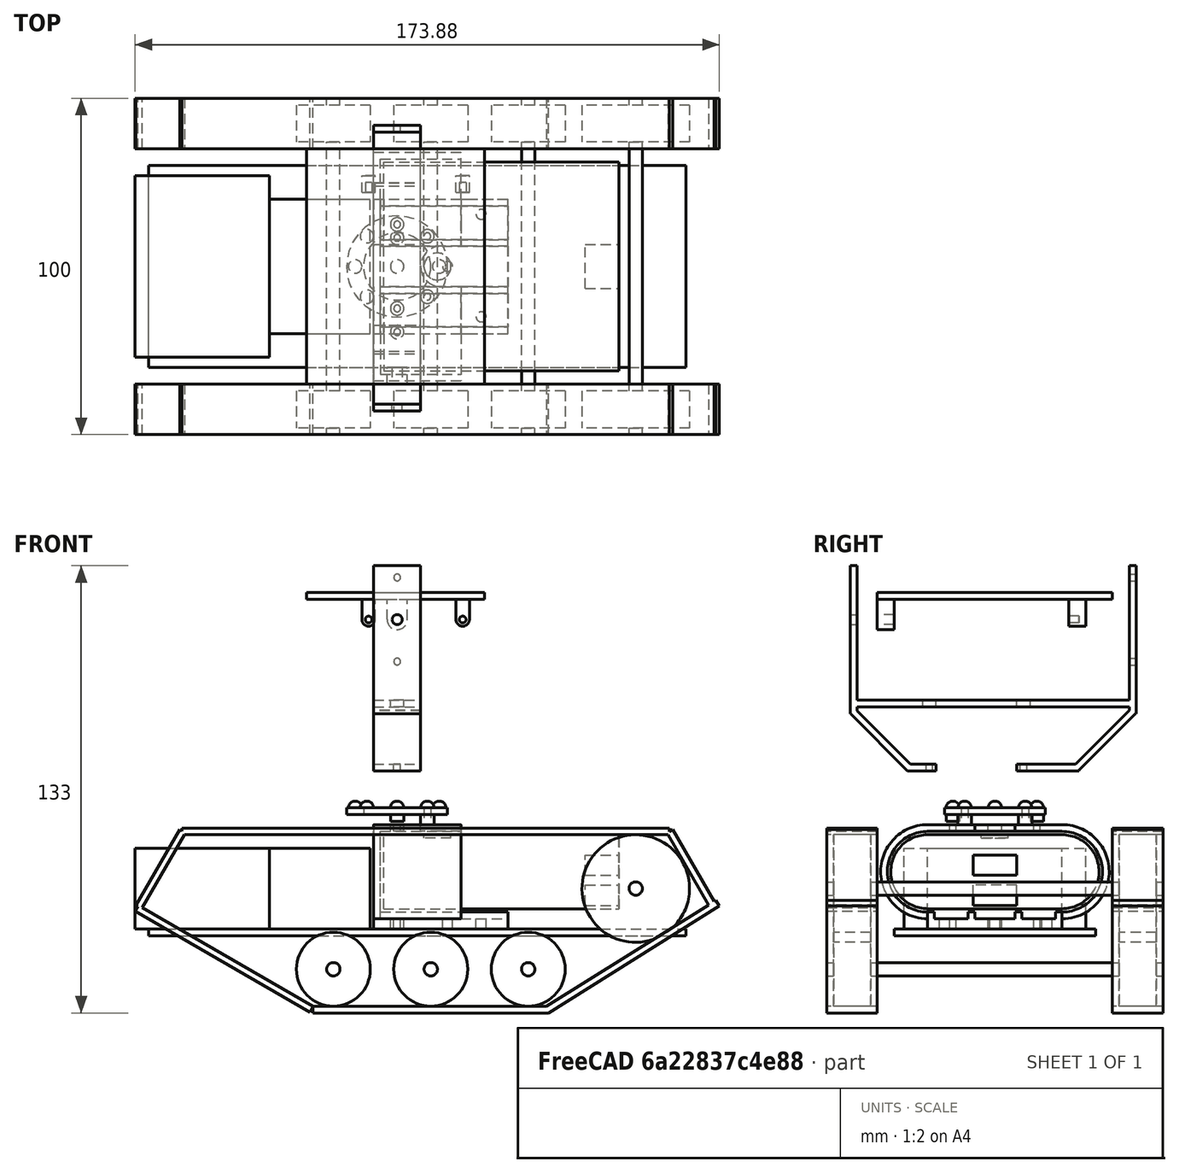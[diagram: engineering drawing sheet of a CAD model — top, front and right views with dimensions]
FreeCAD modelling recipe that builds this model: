
FCSTD DOCUMENT
Label: androidtank_4
License: CC-BY 3.0
LicenseURL: http://creativecommons.org/licenses/by/3.0/
objects: Part::Cylinder×43, Part::Box×31, Part::MultiFuse×17, Part::Sphere×8, Part::Cut×6, App::DocumentObjectGroup×1
note: 105 computed .brp shape members not serialized (recipe doc carries the construction recipe); baked Part::Feature solids carry a one-line shape summary decoded from their .brp

FEATURE [Part::Box] Box  label="MainFrame"
  Height = 2
  Length = 160
  Width = 60
FEATURE [Part::Box] Box001001  label="Moter Unit2"
  Height = 24
  Length = 30
  Placement = pos=(36,10,2) rot=(0,0,1;0rad)
  Width = 40
FEATURE [Part::Cylinder] Cylinder002  label="Wheel1"
  Angle = 360
  Height = 11
  Placement = pos=(20,-7,14) rot=(1,0,0;1.5708rad)
  Radius = 16
FEATURE [Part::Cylinder] Cylinder  label="Shaft"
  Angle = 360
  Height = 100
  Placement = pos=(20,-20,14) rot=(-1,0,0;1.5708rad)
  Radius = 2
FEATURE [Part::Cylinder] Cylinder002001  label="Wheel2"
  Angle = 360
  Height = 11
  Placement = pos=(20,78,14) rot=(1,0,0;1.5708rad)
  Radius = 16
FEATURE [Part::MultiFuse] Fusion001  label="WheelSet2"
  Placement = pos=(125,0,0) rot=(0,0,1;0rad)
  Shapes = -> [Cylinder,Cylinder002,Cylinder002001]
FEATURE [Part::Box] Box001002
  Height = 2
  Length = 145
  Placement = pos=(10,-20,30) rot=(0,0,1;0rad)
  Width = 15
FEATURE [Part::Box] Box001002001
  Height = 2
  Length = 70
  Placement = pos=(49,-20,-23) rot=(0,0,1;0rad)
  Width = 15
FEATURE [Part::Box] Box001002001001
  Height = 2
  Length = 60
  Placement = pos=(119,-20,-23) rot=(0,-1,0;0.558505rad)
  Width = 15
FEATURE [Part::Box] Box001002001002
  Height = 2
  Length = 60
  Placement = pos=(49,-20,-21) rot=(0,1,0;3.66519rad)
  Width = 15
FEATURE [Part::Box] Box001002001003
  Height = 2
  Length = 26
  Placement = pos=(-2,-20,8) rot=(0,-1,0;1.0472rad)
  Width = 15
FEATURE [Part::Box] Box001002001003001
  Height = 2
  Length = 26
  Placement = pos=(169,-20,9) rot=(0,-1,0;2.0944rad)
  Width = 15
FEATURE [Part::MultiFuse] Fusion002001002  label="Caterpiller1"
  Shapes = -> [Box001002,Box001002001,Box001002001002,Box001002001001,Box001002001003,Box001002001003001]
FEATURE [Part::MultiFuse] Fusion002001002001  label="Caterpiller2"
  Placement = pos=(0,85,0) rot=(0,0,1;0rad)
  Shapes = -> [Box001002,Box001002001,Box001002001002,Box001002001001,Box001002001003,Box001002001003001]
FEATURE [Part::Cylinder] Cylinder002001001002  label="Wheel006"
  Angle = 360
  Height = 11
  Placement = pos=(20,78,14) rot=(1,0,0;1.5708rad)
  Radius = 11
FEATURE [Part::Cylinder] Cylinder002001001002001  label="Wheel007"
  Angle = 360
  Height = 11
  Placement = pos=(20,-7,14) rot=(1,0,0;1.5708rad)
  Radius = 11
FEATURE [Part::Cylinder] Cylinder002001002001  label="Shaft002"
  Angle = 360
  Height = 100
  Placement = pos=(20,-20,14) rot=(-1,0,0;1.5708rad)
  Radius = 2
FEATURE [Part::MultiFuse] Fusion002001002002002  label="SWheelSet1"
  Placement = pos=(35,0,-24) rot=(0,0,1;0rad)
  Shapes = -> [Cylinder002001002001,Cylinder002001001002,Cylinder002001001002001]
FEATURE [Part::MultiFuse] Fusion002001002002002001  label="SWheelSet2"
  Placement = pos=(64,0,-24) rot=(0,0,1;0rad)
  Shapes = -> [Cylinder002001002001,Cylinder002001001002,Cylinder002001001002001]
FEATURE [Part::MultiFuse] Fusion002001002002002001001  label="SWheelSet3"
  Placement = pos=(93,0,-24) rot=(0,0,1;0rad)
  Shapes = -> [Cylinder002001002001,Cylinder002001001002,Cylinder002001001002001]
FEATURE [Part::Box] Box001002001003002
  Height = 22
  Length = 70
  Placement = pos=(0,0,-11) rot=(0,0,1;0rad)
  Width = 40
FEATURE [Part::Cylinder] Cylinder002001001002002
  Angle = 360
  Height = 70
  Placement = pos=(0,0,0) rot=(0,1,0;1.5708rad)
  Radius = 11
FEATURE [Part::Cylinder] Cylinder001
  Angle = 360
  Height = 70
  Placement = pos=(0,40,0) rot=(0,1,0;1.5708rad)
  Radius = 11
FEATURE [Part::Cylinder] Cylinder002001001002003  label="PowerButton"
  Angle = 360
  Height = 2
  Placement = pos=(16,20,10) rot=(0,0,1;0rad)
  Radius = 4
FEATURE [Part::Box] Box001002001003003  label="USB1"
  Height = 6
  Length = 15
  Placement = pos=(60,13.5,-1) rot=(0,0,1;0rad)
  Width = 13
FEATURE [Part::Box] Box001001001  label="USB2"
  Height = 6
  Length = 15
  Placement = pos=(60,13.5,-10) rot=(0,0,1;0rad)
  Width = 13
FEATURE [Part::MultiFuse] Fusion002001002002002001002
  Shapes = -> [Cylinder001,Box001002001003002,Cylinder002001001002002]
FEATURE [Part::MultiFuse] Fusion001001
  Shapes = -> [Box001001001,Cylinder002001001002003,Box001002001003003]
FEATURE [Part::Cut] Cut  label="Eneloop"
  Base = -> Fusion002001002002002001002
  Placement = pos=(70,10,19) rot=(0,0,1;0rad)
  Tool = -> Fusion001001
FEATURE [Part::Cylinder] Cylinder001001  label="Cylinder002"
  Angle = 360
  Height = 26
  Placement = pos=(0,50,19) rot=(0,1,0;1.5708rad)
  Radius = 14
FEATURE [Part::Box] Box001002001003002001  label="Box001002001003002001001001001006001001002001003001002"
  Height = 28
  Length = 26
  Placement = pos=(0,10,5) rot=(0,0,1;0rad)
  Width = 40
FEATURE [Part::Cylinder] Cylinder002001001002002001  label="Cylinder003"
  Angle = 360
  Height = 26
  Placement = pos=(0,10,19) rot=(0,1,0;1.5708rad)
  Radius = 14
FEATURE [Part::Box] Box001  label="Moter Unit1"
  Height = 24
  Length = 40
  Placement = pos=(-4,3,2) rot=(0,0,1;0rad)
  Width = 54
FEATURE [App::DocumentObjectGroup] ____________  label="DriveFrame"
  Group = -> [Box,Box001,Box001001,Fusion002001002,Fusion002001002001,Fusion002001002002002,Fusion002001002002002001,Fusion002001002002002001001,Fusion001]
FEATURE [Part::Box] Box001002001003002001001  label="Box003"
  Height = 5
  Length = 40
  Placement = pos=(0,10,2) rot=(0,0,1;0rad)
  Width = 40
FEATURE [Part::Box] Box001002001003002001002  label="Box004"
  Height = 24
  Length = 26
  Placement = pos=(2,10,7) rot=(0,0,1;0rad)
  Width = 40
FEATURE [Part::Cylinder] Cylinder001001001  label="Cylinder004"
  Angle = 360
  Height = 26
  Placement = pos=(2,50,19) rot=(0,1,0;1.5708rad)
  Radius = 12
FEATURE [Part::Cylinder] Cylinder002001001002002001001  label="Cylinder005"
  Angle = 360
  Height = 26
  Placement = pos=(2,10,19) rot=(0,1,0;1.5708rad)
  Radius = 12
FEATURE [Part::Cylinder] Cylinder002001001002003001  label="PowerButton001"
  Angle = 360
  Height = 4
  Placement = pos=(20,30,30) rot=(0,0,1;0rad)
  Radius = 6
FEATURE [Part::Box] Box001002001003002001003  label="Box005"
  Height = 4
  Length = 10
  Placement = pos=(20,24,30) rot=(0,0,1;0rad)
  Width = 12
FEATURE [Part::Box] Box001002001003002001001001  label="Box006"
  Height = 3
  Length = 40
  Placement = pos=(2,12,5) rot=(0,0,1;0rad)
  Width = 10
FEATURE [Part::Box] Box001002001003002001001001001  label="Box007"
  Height = 3
  Length = 40
  Placement = pos=(2,24,5) rot=(0,0,1;0rad)
  Width = 12
FEATURE [Part::Box] Box001002001003002001001001001001  label="Box008"
  Height = 3
  Length = 40
  Placement = pos=(2,38,5) rot=(0,0,1;0rad)
  Width = 10
FEATURE [Part::MultiFuse] Fusion002001002002002001003
  Shapes = -> [Box001002001003002001,Cylinder001001,Cylinder002001001002002001,Box001002001003002001001]
FEATURE [Part::MultiFuse] Fusion002001002002002001004
  Shapes = -> [Box001002001003002001002,Cylinder002001001002002001001,Cylinder001001001,Box001002001003002001001001001001,Box001002001003002001001001001,Box001002001003002001001001,Box001002001003002001003,Cylinder002001001002003001]
FEATURE [Part::Cut] Cut001  label="BatteryFrame"
  Base = -> Fusion002001002002002001003
  Placement = pos=(67,0,0) rot=(0,0,1;0rad)
  Tool = -> Fusion002001002002002001004
FEATURE [Part::Cylinder] Cylinder002001001002002001002001  label="Cylinder007"
  Angle = 360
  Height = 40
  Placement = pos=(74,17.5,0) rot=(0,0,1;0rad)
  Radius = 1
FEATURE [Part::Cylinder] Cylinder002001001002002001002  label="Cylinder006"
  Angle = 360
  Height = 40
  Placement = pos=(74,42.5,0) rot=(0,0,1;0rad)
  Radius = 1
FEATURE [Part::Cylinder] Cylinder002001001002002001002001001  label="Cylinder008"
  Angle = 360
  Height = 40
  Placement = pos=(89,30,0) rot=(0,0,1;0rad)
  Radius = 1.5
FEATURE [Part::Cylinder] Cylinder002001001002002001002001002  label="Cylinder009"
  Angle = 360
  Height = 40
  Placement = pos=(99,45.5,0) rot=(0,0,1;0rad)
  Radius = 1.5
FEATURE [Part::Cylinder] Cylinder002001001002002001002001003  label="Cylinder0010"
  Angle = 360
  Height = 40
  Placement = pos=(99,15,0) rot=(0,0,1;0rad)
  Radius = 1.5
FEATURE [Part::Box] Box001002001003002001001001001006  label="Box009"
  Height = 2
  Length = 53
  Placement = pos=(47,-5,100) rot=(0,0,1;0rad)
  Width = 70
FEATURE [Part::Box] Box001002001003002001001001001006001  label="Box010"
  Height = 44
  Length = 14
  Placement = pos=(67,70,66) rot=(0,0,1;0rad)
  Width = 2
FEATURE [Part::Box] Box001002001003002001001001001006001001  label="Box011"
  Height = 2
  Length = 13
  Placement = pos=(67.5,12.5,48) rot=(0,0,1;0rad)
  Width = 23.5
FEATURE [Part::Box] Box001002001003002001001001001006001001001  label="Box012"
  Height = 44
  Length = 14
  Placement = pos=(67,-13,66) rot=(0,0,1;0rad)
  Width = 2
FEATURE [Part::Cylinder] Cylinder002001001002002001002001008  label="Hole1"
  Angle = 360
  Height = 20
  Placement = pos=(74,-20,94) rot=(-1,0,0;1.5708rad)
  Radius = 1.5
FEATURE [Part::Cylinder] Cylinder002001001002002001002001008001  label="Hole2"
  Angle = 360
  Height = 20
  Placement = pos=(74,60,106.5) rot=(-1,0,0;1.5708rad)
  Radius = 1
FEATURE [Part::Cylinder] Cylinder002001001002002001002001008001001  label="Hole4"
  Angle = 360
  Height = 20
  Placement = pos=(74,38.5,41) rot=(0,0,1;0rad)
  Radius = 1
FEATURE [Part::Cylinder] Cylinder002001001002002001002001008001001001  label="Hole3"
  Angle = 360
  Height = 20
  Placement = pos=(74,60,81.5) rot=(-1,0,0;1.5708rad)
  Radius = 1
FEATURE [Part::Cylinder] Cylinder002001001002002001002001008001001002  label="Hole5"
  Angle = 360
  Height = 20
  Placement = pos=(74,10.5,41) rot=(0,0,1;0rad)
  Radius = 1
FEATURE [Part::Box] Box001002001003002001001001001006001001001001  label="Box013"
  Height = 24
  Length = 14
  Placement = pos=(67,4,49) rot=(1,0,0;0.785397rad)
  Width = 2
FEATURE [Part::Box] Box001002001003002001001001001006001001001001001  label="Box014"
  Height = 24
  Length = 14
  Placement = pos=(67,53.41,50.41) rot=(-1,0,0;0.785397rad)
  Width = 2
FEATURE [Part::Box] Box001002001003002001001001001006001001002001  label="Box016"
  Height = 2
  Length = 14
  Placement = pos=(67,4,49) rot=(0,0,1;0rad)
  Width = 8.5
FEATURE [Part::Box] Box001002001003002001001001001006001001002001001  label="Box017"
  Height = 2
  Length = 14
  Placement = pos=(67,36.5,49) rot=(0,0,1;0rad)
  Width = 18.5
FEATURE [Part::Box] Box001002001003002001001001001006001001002001002  label="Box015"
  Height = 2
  Length = 14
  Placement = pos=(67,-13,68) rot=(0,0,1;0rad)
  Width = 85
FEATURE [Part::MultiFuse] Fusion002001002002002001009
  Shapes = -> [Box001002001003002001001001001006001,Box001002001003002001001001001006001001001001,Box001002001003002001001001001006001001001,Box001002001003002001001001001006001001001001001,Box001002001003002001001001001006001001002001,Box001002001003002001001001001006001001002001002,Box001002001003002001001001001006001001002001001]
FEATURE [Part::Cylinder] Cylinder002001001002002001002001008001001002001  label="Hole006"
  Angle = 360
  Height = 20
  Placement = pos=(74,10.5,60) rot=(0,0,1;0rad)
  Radius = 2
FEATURE [Part::Cylinder] Cylinder002001001002002001002001008001001002002  label="Hole007"
  Angle = 360
  Height = 20
  Placement = pos=(74,38.5,60) rot=(0,0,1;0rad)
  Radius = 2
FEATURE [Part::MultiFuse] Fusion002001002002002001010
  Shapes = -> [Cylinder002001001002002001002001008001,Box001002001003002001001001001006001001,Cylinder002001001002002001002001008001001,Cylinder002001001002002001002001008,Cylinder002001001002002001002001008001001001,Cylinder002001001002002001002001008001001002,Cylinder002001001002002001002001008001001002002,Cylinder002001001002002001002001008001001002001]
FEATURE [Part::Cut] Cut003  label="HeadFrame"
  Base = -> Fusion002001002002002001009
  Tool = -> Fusion002001002002002001010
FEATURE [Part::Cylinder] Cylinder003001001  label="Cylinder002001001002002001002001008001001002005"
  Angle = 360
  Height = 4
  Placement = pos=(-6.5,6,25) rot=(0,0,1;0rad)
  Radius = 2
FEATURE [Part::Cylinder] Cylinder003001001001  label="Cylinder002001001002002001002001008001001002006"
  Angle = 360
  Height = 4
  Placement = pos=(18.5,6,25) rot=(0,0,1;0rad)
  Radius = 2
FEATURE [Part::Cylinder] Cylinder003001001003  label="Cylinder002001001002002001002001008001001002007"
  Angle = 360
  Height = 2
  Placement = pos=(6,6,25) rot=(0,0,1;0rad)
  Radius = 15
FEATURE [Part::Sphere] Sphere
  Angle1 = -90
  Angle2 = 0
  Angle3 = 360
  Placement = pos=(-3,-3,25) rot=(0,0,1;0rad)
  Radius = 2
FEATURE [Part::Sphere] Sphere001
  Angle1 = -90
  Angle2 = 0
  Angle3 = 360
  Placement = pos=(15,-3,25) rot=(0,0,1;0rad)
  Radius = 2
FEATURE [Part::Sphere] Sphere001001  label="Sphere002"
  Angle1 = -90
  Angle2 = 0
  Angle3 = 360
  Placement = pos=(15,15,25) rot=(0,0,1;0rad)
  Radius = 2
FEATURE [Part::Sphere] Sphere001001001  label="Sphere003"
  Angle1 = -90
  Angle2 = 0
  Angle3 = 360
  Placement = pos=(-3,15,25) rot=(0,0,1;0rad)
  Radius = 2
FEATURE [Part::Cylinder] Cylinder003001001005001003  label="Cylinder018"
  Angle = 360
  Height = 5
  Placement = pos=(-3,-3,25) rot=(0,0,1;0rad)
  Radius = 2
FEATURE [Part::Cylinder] Cylinder003001001001002  label="Cylinder019"
  Angle = 360
  Height = 5
  Placement = pos=(15,-3,25) rot=(0,0,1;0rad)
  Radius = 2
FEATURE [Part::Cylinder] Cylinder003001001005001004  label="Cylinder020"
  Angle = 360
  Height = 4
  Placement = pos=(-6.5,6,25) rot=(0,0,1;0rad)
  Radius = 1
FEATURE [Part::Cylinder] Cylinder003001001001003  label="Cylinder021"
  Angle = 360
  Height = 4
  Placement = pos=(18.5,6,25) rot=(0,0,1;0rad)
  Radius = 1
FEATURE [Part::Cylinder] Cylinder003001001005001003001  label="Cylinder022"
  Angle = 360
  Height = 5
  Placement = pos=(-3,-3,25) rot=(0,0,1;0rad)
  Radius = 1
FEATURE [Part::Cylinder] Cylinder003001001001002001  label="Cylinder023"
  Angle = 360
  Height = 5
  Placement = pos=(15,-3,25) rot=(0,0,1;0rad)
  Radius = 1
FEATURE [Part::Sphere] Sphere001001001001  label="Sphere004"
  Angle1 = -90
  Angle2 = 0
  Angle3 = 360
  Placement = pos=(-6.5,6,25) rot=(0,0,1;0rad)
  Radius = 2
FEATURE [Part::Sphere] Sphere001001001001001  label="Sphere005"
  Angle1 = -90
  Angle2 = 0
  Angle3 = 360
  Placement = pos=(18.5,6,25) rot=(0,0,1;0rad)
  Radius = 2
FEATURE [Part::Sphere] Sphere001001001001001001  label="Sphere006"
  Angle1 = -90
  Angle2 = 0
  Angle3 = 360
  Placement = pos=(6,-6.5,25) rot=(0,0,1;0rad)
  Radius = 2
FEATURE [Part::Sphere] Sphere001001001001001001001  label="Sphere007"
  Angle1 = -90
  Angle2 = 0
  Angle3 = 360
  Placement = pos=(6,18.5,25) rot=(0,0,1;0rad)
  Radius = 2
FEATURE [Part::MultiFuse] Fusion012
  Shapes = -> [Cylinder003001001,Sphere,Cylinder003001001003,Cylinder003001001001002,Cylinder003001001001,Sphere001001001,Sphere001001001001001001,Sphere001001001001,Sphere001,Sphere001001,Cylinder003001001005001003,Sphere001001001001001001001,Sphere001001001001001]
FEATURE [Part::Cylinder] Cylinder003001001003001  label="Cylinder024"
  Angle = 360
  Height = 2
  Placement = pos=(6,6,25) rot=(0,0,1;0rad)
  Radius = 10
FEATURE [Part::MultiFuse] Fusion013
  Shapes = -> [Cylinder003001001003001,Cylinder003001001005001003001,Cylinder003001001001002001,Cylinder003001001005001004,Cylinder003001001001003]
FEATURE [Part::Cut] Cut002002  label="Guide2"
  Base = -> Fusion012
  Placement = pos=(80,36,63) rot=(0.707107,-0.707107,0;3.14159rad)
  Tool = -> Fusion013
FEATURE [Part::Cylinder] Cylinder002001001002002001002001008001001002003  label="Cylinder025"
  Angle = 360
  Height = 5
  Placement = pos=(74,0,94) rot=(1,0,0;1.5708rad)
  Radius = 3
FEATURE [Part::Box] Box001002001003002001001001001006001001002001003  label="Box020"
  Height = 6
  Length = 6
  Placement = pos=(71,-5,94) rot=(0,0,1;0rad)
  Width = 5
FEATURE [Part::Cylinder] Cylinder002001001002002001002001008001001002003001  label="Cylinder026"
  Angle = 360
  Height = 7
  Placement = pos=(74,1,94) rot=(1,0,0;1.5708rad)
  Radius = 1.5
FEATURE [Part::Box] Box001002001003002001001001001006001001002001003001001  label="Box022"
  Height = 6
  Length = 4
  Placement = pos=(91.5,52,94) rot=(0,0,1;0rad)
  Width = 5
FEATURE [Part::Cylinder] Cylinder002001001002002001002001008001001002003002  label="Cylinder027"
  Angle = 360
  Height = 5
  Placement = pos=(65.5,57,94) rot=(1,0,0;1.5708rad)
  Radius = 2
FEATURE [Part::Cylinder] Cylinder002001001002002001002001008001001002003002001  label="Cylinder028"
  Angle = 360
  Height = 5
  Placement = pos=(93.5,57,94) rot=(1,0,0;1.5708rad)
  Radius = 2
FEATURE [Part::Box] Box001002001003002001001001001006001001002001003001  label="Box021"
  Height = 6
  Length = 4
  Placement = pos=(63.5,52,94) rot=(0,0,1;0rad)
  Width = 5
FEATURE [Part::Cylinder] Cylinder002001001002002001002001008001001002003002002  label="Cylinder029"
  Angle = 360
  Height = 5
  Placement = pos=(65.5,55,94) rot=(1,0,0;1.5708rad)
  Radius = 1
FEATURE [Part::Cylinder] Cylinder002001001002002001002001008001001002003002001001  label="Cylinder030"
  Angle = 360
  Height = 5
  Placement = pos=(93.5,55,94) rot=(1,0,0;1.5708rad)
  Radius = 1
FEATURE [Part::MultiFuse] Fusion002001002002002001011
  Shapes = -> [Box001002001003002001001001001006,Box001002001003002001001001001006001001002001003001001,Cylinder002001001002002001002001008001001002003002001,Box001002001003002001001001001006001001002001003,Cylinder002001001002002001002001008001001002003,Box001002001003002001001001001006001001002001003001,Cylinder002001001002002001002001008001001002003002]
FEATURE [Part::MultiFuse] Fusion002001002002002001012
  Shapes = -> [Cylinder002001001002002001002001008001001002003001,Cylinder002001001002002001002001008001001002003002002,Cylinder002001001002002001002001008001001002003002001001]
FEATURE [Part::Cut] Cut002003  label="HeadMount"
  Base = -> Fusion002001002002002001011
  Tool = -> Fusion002001002002002001012
FEATURE [Part::Cylinder] Cylinder002001001002002001002001001001  label="Cylinder040"
  Angle = 360
  Height = 40
  Placement = pos=(74,30,0) rot=(0,0,1;0rad)
  Radius = 2
FEATURE [Part::MultiFuse] Fusion002001002002002001013  label="BatteryFrameHoles"
  Shapes = -> [Cylinder002001001002002001002001,Cylinder002001001002002001002,Cylinder002001001002002001002001001,Cylinder002001001002002001002001002,Cylinder002001001002002001002001003,Cylinder002001001002002001002001001001]
FEATURE [Part::Cut] Cut002004  label="BatteryFrame2"
  Base = -> Cut001
  Tool = -> Fusion002001002002002001013
